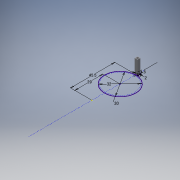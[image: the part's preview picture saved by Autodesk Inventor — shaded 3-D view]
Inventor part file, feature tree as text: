
AUTODESK INVENTOR PART (.ipt)
format: ipt  version: 2016 (Build 200138000, 138)  size: 105,472 bytes
history: native  units: mm
features: extrude x2, other x1, sketch x1
ambient origin geometry x8: Origin, YZ Plane, XZ Plane, XY Plane, X Axis, Y Axis, Z Axis, Center Point
bodies: Body1 (feature_tree)
feature tree (4):
  other  "ソリッド1"
  sketch  "スケッチ1"
  extrude  "押し出し1"  Depth=32.0mm
  extrude  "押し出し3"  Depth=2.0mm
